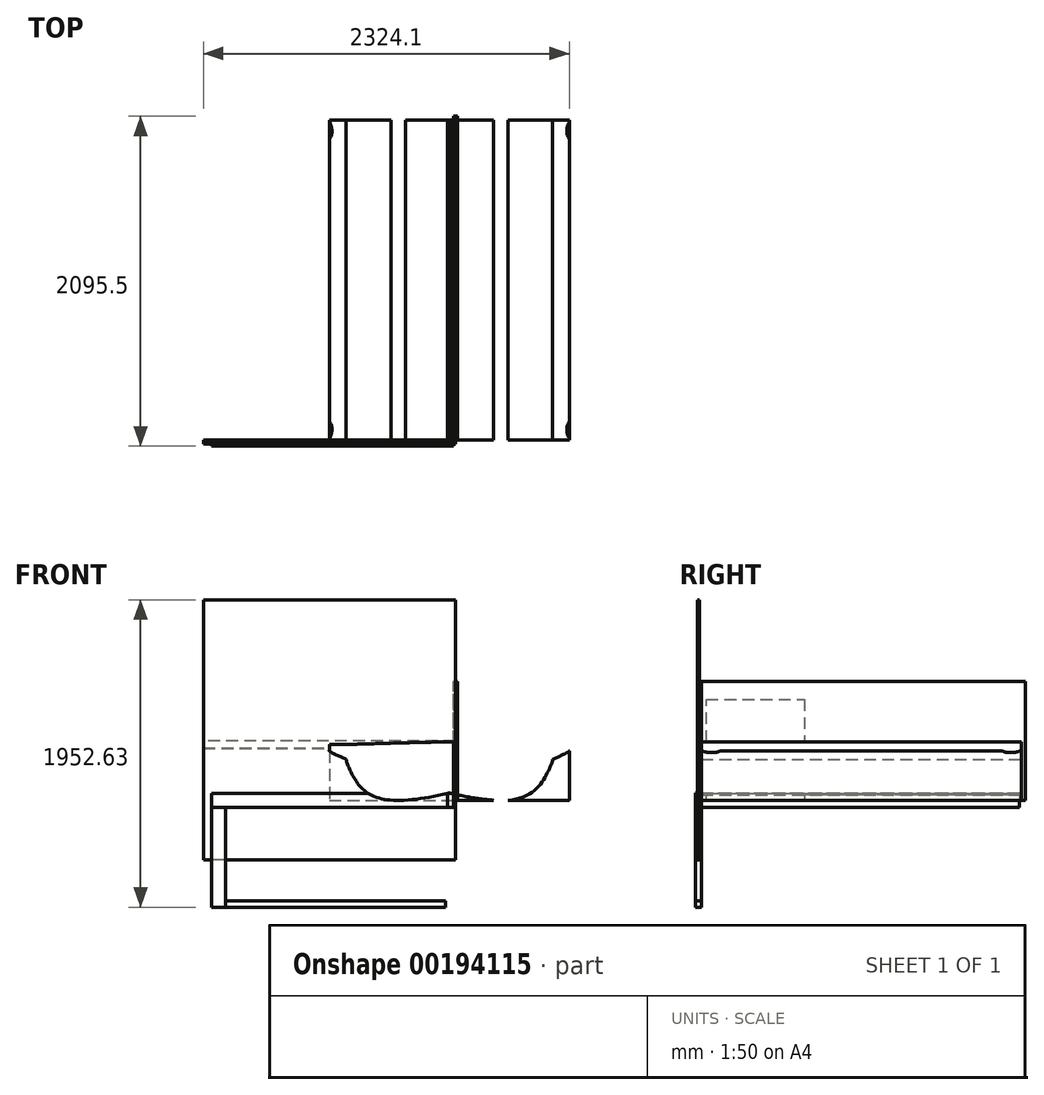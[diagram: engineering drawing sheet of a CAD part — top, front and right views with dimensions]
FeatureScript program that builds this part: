
annotation { "Feature Type Name" : "Feature", "Feature Type Description" : "" }
export const myFeature = defineFeature(function(context is Context, id is Id, definition is map)
    precondition{}
    {
        {
            var Q0;
            Q0=qCreatedBy(makeId("Front.planeOp"),FACE);
            var sketch = newSketch(context, id + "F0", { "sketchPlane" : qUnion([Q0])});
            skLineSegment(sketch, "E0.bottom", {"start": v(749.3, 44.45) * mm, "end": v(-749.3, 44.45) * mm});
            skLineSegment(sketch, "E0.top", {"start": v(749.3, -44.45) * mm, "end": v(-749.3, -44.45) * mm});
            skLineSegment(sketch, "E0.left", {"start": v(749.3, 44.45) * mm, "end": v(749.3, -44.45) * mm});
            skLineSegment(sketch, "E0.right", {"start": v(-749.3, 44.45) * mm, "end": v(-749.3, -44.45) * mm});
            skPoint(sketch, "E0.middle", {"position": v(0, 0) * mm});
            skSolve(sketch);
        }
        {
            var Q0;
            Q0 = qSketchRegion(id + "F0", true);
            extrude(context, id + "F1", {"entities" : qUnion([Q0]), "depth" : 38.1 * mm});
        }
        {
            var Q0;
            Q0=makeQuery(id+"F1.opExtrude","SWEPT_FACE",FACE,{"disambiguationData":[OSD([sQuery(id+"F0.wireOp",EDGE,"E0.left")])]});
            var sketch = newSketch(context, id + "F2", { "sketchPlane" : qUnion([Q0])});
            skLineSegment(sketch, "E1.bottom", {"start": v(-38.1, 44.45) * mm, "end": v(2019.3, 44.45) * mm});
            skLineSegment(sketch, "E1.top", {"start": v(-38.1, -44.45) * mm, "end": v(2019.3, -44.45) * mm});
            skLineSegment(sketch, "E1.left", {"start": v(-38.1, 44.45) * mm, "end": v(-38.1, -44.45) * mm});
            skLineSegment(sketch, "E1.right", {"start": v(2019.3, 44.45) * mm, "end": v(2019.3, -44.45) * mm});
            skSolve(sketch);
        }
        {
            var Q0;
            Q0 = qSketchRegion(id + "F2", true);
            extrude(context, id + "F3", {"entities" : qUnion([Q0]), "depth" : 38.1 * mm});
        }
        {
            var Q0;
            Q0=makeQuery(id+"F1.opExtrude","CAP_FACE",FACE,{"disambiguationData":[OSD([sQuery(id+"F0.wireOp",EDGE,"E0.bottom"),sQuery(id+"F0.wireOp",EDGE,"E0.top"),sQuery(id+"F0.wireOp",EDGE,"E0.left"),sQuery(id+"F0.wireOp",EDGE,"E0.right")])],"isStart":false});
            var sketch = newSketch(context, id + "F4", { "sketchPlane" : qUnion([Q0])});
            skLineSegment(sketch, "E2.bottom", {"start": v(-749.3, -44.45) * mm, "end": v(-660.4, -44.45) * mm});
            skLineSegment(sketch, "E2.top", {"start": v(-749.3, -679.45) * mm, "end": v(-660.4, -679.45) * mm});
            skLineSegment(sketch, "E2.left", {"start": v(-749.3, -44.45) * mm, "end": v(-749.3, -679.45) * mm});
            skLineSegment(sketch, "E2.right", {"start": v(-660.4, -44.45) * mm, "end": v(-660.4, -679.45) * mm});
            skSolve(sketch);
        }
        {
            var Q0;
            Q0 = qSketchRegion(id + "F4", true);
            extrude(context, id + "F5", {"entities" : qUnion([Q0]), "oppositeDirection" : true, "depth" : 38.1 * mm});
        }
        {
            var Q0;
            Q0=makeQuery(id+"F5.opExtrude","CAP_FACE",FACE,{"disambiguationData":[OSD([sQuery(id+"F4.wireOp",EDGE,"E2.bottom"),sQuery(id+"F4.wireOp",EDGE,"E2.top"),sQuery(id+"F4.wireOp",EDGE,"E2.left"),sQuery(id+"F4.wireOp",EDGE,"E2.right")])],"isStart":true});
            var sketch = newSketch(context, id + "F6", { "sketchPlane" : qUnion([Q0])});
            skLineSegment(sketch, "E3.bottom", {"start": v(-660.4, -679.45) * mm, "end": v(736.6, -679.45) * mm});
            skLineSegment(sketch, "E3.top", {"start": v(-660.4, -638.17) * mm, "end": v(736.6, -638.17) * mm});
            skLineSegment(sketch, "E3.left", {"start": v(-660.4, -679.45) * mm, "end": v(-660.4, -638.17) * mm});
            skLineSegment(sketch, "E3.right", {"start": v(736.6, -679.45) * mm, "end": v(736.6, -638.17) * mm});
            skSolve(sketch);
        }
        {
            var Q0;
            Q0=makeQuery(id+"F6.imprint","IMPRINT",FACE,{"disambiguationData":[TD([[makeQuery(id+"F6.imprint","IMPRINT",EDGE,{"derivedFrom":sQuery(id+"F6.wireOp",EDGE,"E3.bottom")}),1.0]])]});
            extrude(context, id + "F7", {"entities" : qUnion([Q0]), "oppositeDirection" : true, "depth" : 38.1 * mm});
        }
        {
            var Q0;
            Q0=makeQuery(id+"F3.opExtrude","CAP_FACE",FACE,{"disambiguationData":[OSD([sQuery(id+"F2.wireOp",EDGE,"E1.bottom"),sQuery(id+"F2.wireOp",EDGE,"E1.top"),sQuery(id+"F2.wireOp",EDGE,"E1.left"),sQuery(id+"F2.wireOp",EDGE,"E1.right")])],"isStart":false});
            var sketch = newSketch(context, id + "F8", { "sketchPlane" : qUnion([Q0])});
            skLineSegment(sketch, "E4", {"start": v(0, 0) * mm, "end": v(0, 755.65) * mm});
            skLineSegment(sketch, "E5", {"start": v(0, 755.65) * mm, "end": v(2057.4, 755.65) * mm});
            skLineSegment(sketch, "E6", {"start": v(0, 0) * mm, "end": v(31.75, 0) * mm});
            skLineSegment(sketch, "E7", {"start": v(31.75, 0) * mm, "end": v(31.75, 641.35) * mm});
            skLineSegment(sketch, "E8", {"start": v(31.75, 641.35) * mm, "end": v(654.05, 641.35) * mm});
            skLineSegment(sketch, "E9", {"start": v(654.05, 641.35) * mm, "end": v(654.05, 0) * mm});
            skLineSegment(sketch, "E10", {"start": v(654.05, 0) * mm, "end": v(2057.4, 0) * mm});
            skPoint(sketch, "E10.endSnap0", {"position": v(2019.3, 0) * mm});
            skLineSegment(sketch, "E11", {"start": v(2057.4, 0) * mm, "end": v(2057.4, 755.65) * mm});
            skSolve(sketch);
        }
        {
            var Q0;
            Q0 = qSketchRegion(id + "F8", true);
            extrude(context, id + "F9", {"entities" : qUnion([Q0]), "depth" : 12.7 * mm});
        }
        {
            var Q0;
            Q0=makeQuery(id+"F9.opExtrude","CAP_FACE",FACE,{"disambiguationData":[OSD([sQuery(id+"F8.wireOp",EDGE,"E4"),sQuery(id+"F8.wireOp",EDGE,"E5"),sQuery(id+"F8.wireOp",EDGE,"E6"),sQuery(id+"F8.wireOp",EDGE,"E7"),sQuery(id+"F8.wireOp",EDGE,"E8"),sQuery(id+"F8.wireOp",EDGE,"E9"),sQuery(id+"F8.wireOp",EDGE,"E10"),sQuery(id+"F8.wireOp",EDGE,"E11")])],"isStart":false});
            var sketch = newSketch(context, id + "F10", { "sketchPlane" : qUnion([Q0])});
            skLineSegment(sketch, "E12.bottom", {"start": v(0, 755.65) * mm, "end": v(2057.4, 755.65) * mm});
            skLineSegment(sketch, "E12.top", {"start": v(0, 0) * mm, "end": v(2057.4, 0) * mm});
            skLineSegment(sketch, "E12.left", {"start": v(0, 755.65) * mm, "end": v(0, 0) * mm});
            skLineSegment(sketch, "E12.right", {"start": v(2057.4, 755.65) * mm, "end": v(2057.4, 0) * mm});
            skSolve(sketch);
        }
        {
            var Q0;
            Q0 = qSketchRegion(id + "F10", true);
            extrude(context, id + "F11", {"entities" : qUnion([Q0]), "depth" : 12.7 * mm});
        }
        {
            var Q0;
            Q0=qCreatedBy(makeId("Front.planeOp"),FACE);
            var sketch = newSketch(context, id + "F12", { "sketchPlane" : qUnion([Q0])});
            skLineSegment(sketch, "E13.bottom", {"start": v(800.1, 377.83) * mm, "end": v(-800.1, 377.83) * mm});
            skLineSegment(sketch, "E13.top", {"start": v(800.1, -377.83) * mm, "end": v(-800.1, -377.83) * mm});
            skLineSegment(sketch, "E13.left", {"start": v(800.1, 377.83) * mm, "end": v(800.1, -377.83) * mm});
            skLineSegment(sketch, "E13.right", {"start": v(-800.1, 377.83) * mm, "end": v(-800.1, -377.83) * mm});
            skPoint(sketch, "E13.middle", {"position": v(0, 0) * mm});
            skSolve(sketch);
        }
        {
            var Q0;
            Q0 = qSketchRegion(id + "F12", true);
            extrude(context, id + "F13", {"entities" : qUnion([Q0]), "depth" : 12.7 * mm});
        }
        {
            var Q0;
            Q0=makeQuery(id+"F13.opExtrude","CAP_FACE",FACE,{"disambiguationData":[OSD([sQuery(id+"F12.wireOp",EDGE,"E13.bottom"),sQuery(id+"F12.wireOp",EDGE,"E13.top"),sQuery(id+"F12.wireOp",EDGE,"E13.left"),sQuery(id+"F12.wireOp",EDGE,"E13.right")])],"isStart":false});
            var sketch = newSketch(context, id + "F14", { "sketchPlane" : qUnion([Q0])});
            skLineSegment(sketch, "E14.bottom", {"start": v(-800.1, -377.83) * mm, "end": v(800.1, -377.83) * mm});
            skLineSegment(sketch, "E14.top", {"start": v(-800.1, 1273.18) * mm, "end": v(800.1, 1273.18) * mm});
            skLineSegment(sketch, "E14.left", {"start": v(-800.1, -377.83) * mm, "end": v(-800.1, 1273.18) * mm});
            skLineSegment(sketch, "E14.right", {"start": v(800.1, -377.83) * mm, "end": v(800.1, 1273.18) * mm});
            skSolve(sketch);
        }
        {
            var Q0;
            Q0 = qSketchRegion(id + "F14", true);
            extrude(context, id + "F15", {"entities" : qUnion([Q0]), "depth" : 12.7 * mm});
        }
        {
            var Q0;
            Q0=makeQuery(id+"F3.opExtrude","SWEPT_FACE",FACE,{"disambiguationData":[OSD([sQuery(id+"F2.wireOp",EDGE,"E1.bottom")])]});
            var sketch = newSketch(context, id + "F16", { "sketchPlane" : qUnion([Q0])});
            skLineSegment(sketch, "E15.bottom", {"start": v(787.4, -38.1) * mm, "end": v(749.3, -38.1) * mm});
            skLineSegment(sketch, "E15.top", {"start": v(787.4, 2019.3) * mm, "end": v(749.3, 2019.3) * mm});
            skLineSegment(sketch, "E15.left", {"start": v(787.4, -38.1) * mm, "end": v(787.4, 2019.3) * mm});
            skLineSegment(sketch, "E15.right", {"start": v(749.3, -38.1) * mm, "end": v(749.3, 2019.3) * mm});
            skSolve(sketch);
        }
        {
            var Q0;
            Q0 = qSketchRegion(id + "F16", true);
            extrude(context, id + "F17", {"entities" : qUnion([Q0]), "depth" : 19.05 * mm});
        }
        {
            var Q0;
            Q0=qCreatedBy(makeId("Top.planeOp"),FACE);
            var sketch = newSketch(context, id + "F18", { "sketchPlane" : qUnion([Q0])});
            skLineSegment(sketch, "E16.bottom", {"start": v(0, 0) * mm, "end": v(1524, 0) * mm});
            skLineSegment(sketch, "E16.top", {"start": v(0, 2032) * mm, "end": v(1524, 2032) * mm});
            skLineSegment(sketch, "E16.left", {"start": v(0, 0) * mm, "end": v(0, 2032) * mm});
            skLineSegment(sketch, "E16.right", {"start": v(1524, 0) * mm, "end": v(1524, 2032) * mm});
            skSolve(sketch);
        }
        {
            var Q0;
            Q0 = qSketchRegion(id + "F18", true);
            extrude(context, id + "F19", {"entities" : qUnion([Q0]), "depth" : 355.6 * mm});
        }
        {
            var Q0;
            Q0=makeQuery(id+"F19.opExtrude","SWEPT_FACE",FACE,{"disambiguationData":[OSD([sQuery(id+"F18.wireOp",EDGE,"E16.top")])]});
            var sketch = newSketch(context, id + "F20", { "sketchPlane" : qUnion([Q0])});
            skLineSegment(sketch, "E17.bottom", {"start": v(-1524, 355.6) * mm, "end": v(-1361.72, 355.6) * mm});
            skLineSegment(sketch, "E17.left", {"start": v(-1524, 355.6) * mm, "end": v(-1524, 319.78) * mm});
            skFitSpline(sketch, "E18", {"points": [v(-1524, 319.78) * mm, v(-1516.64, 336.7) * mm, v(-1478.51, 351.64) * mm, v(-1361.72, 355.6) * mm, v(-135.1, 312.29) * mm, v(-126.97, 200.76) * mm, v(-389.88, 0) * mm, v(-1524, 312.87) * mm, v(-1524, 319.78) * mm]});
            skLineSegment(sketch, "E19", {"start": v(-762, 0) * mm, "end": v(-762, 388.78) * mm, "construction": true});
            skPoint(sketch, "E19.endSnap0", {"position": v(-762, 355.6) * mm});
            skLineSegment(sketch, "E20.MirrorCS", {"start": v(0, 355.6) * mm, "end": v(-162.28, 355.6) * mm});
            skLineSegment(sketch, "E21.MirrorCS", {"start": v(0, 355.6) * mm, "end": v(0, 319.78) * mm});
            skFitSpline(sketch, "E22.MirrorCS", {"points": [v(0, 319.78) * mm, v(-7.36, 336.7) * mm, v(-45.49, 351.64) * mm, v(-162.28, 355.6) * mm, v(-1388.9, 312.29) * mm, v(-1397.03, 200.76) * mm, v(-1134.12, 0) * mm, v(0, 312.87) * mm, v(0, 319.78) * mm]});
            skSolve(sketch);
        }
        {
            var Q0;
            Q0 = qSketchRegion(id + "F20", true);
            extrude(context, id + "F21", {"entities" : qUnion([Q0]), "operationType" : NewBodyOperationType.REMOVE, "endBound" : BoundingType.THROUGH_ALL, "oppositeDirection" : true, "depth" : 25.4 * mm});
        }
        {
            var Q0;
            Q0=makeQuery(id+"F19.opExtrude","SWEPT_FACE",FACE,{"disambiguationData":[OSD([sQuery(id+"F18.wireOp",EDGE,"E16.right")])]});
            var sketch = newSketch(context, id + "F22", { "sketchPlane" : qUnion([Q0])});
            skLineSegment(sketch, "E23.0", {"start": v(0, 355.6) * mm, "end": v(47.79, 355.6) * mm});
            skLineSegment(sketch, "E24", {"start": v(0, 355.6) * mm, "end": v(0, 333.6) * mm});
            skFitSpline(sketch, "E25", {"points": [v(0, 333.6) * mm, v(5.1, 347.61) * mm, v(47.79, 355.6) * mm, v(79.64, 355.6) * mm, v(118.18, 355.6) * mm, v(129.65, 337.42) * mm, v(112.76, 309.4) * mm, v(21.99, 307.48) * mm, v(2.56, 319.78) * mm, v(0, 329.63) * mm, v(0, 333.6) * mm]});
            skPoint(sketch, "E26.trimOffspring.end.orphan", {"position": v(2032, 355.6) * mm});
            skPoint(sketch, "E27.orphan", {"position": v(0, 303.66) * mm});
            skLineSegment(sketch, "E28", {"start": v(1016, 0) * mm, "end": v(1016, 319.78) * mm, "construction": true});
            skLineSegment(sketch, "E29.MirrorCS", {"start": v(2032, 355.6) * mm, "end": v(2032, 333.6) * mm});
            skFitSpline(sketch, "E30.MirrorCS", {"points": [v(2032, 333.6) * mm, v(2026.9, 347.61) * mm, v(1984.21, 355.6) * mm, v(1952.36, 355.6) * mm, v(1913.82, 355.6) * mm, v(1902.35, 337.42) * mm, v(1919.24, 309.4) * mm, v(2010.01, 307.48) * mm, v(2029.44, 319.78) * mm, v(2032, 329.63) * mm, v(2032, 333.6) * mm]});
            skLineSegment(sketch, "E31.MirrorCS", {"start": v(2032, 355.6) * mm, "end": v(1984.21, 355.6) * mm});
            skPoint(sketch, "E32.MirrorP", {"position": v(2032, 303.66) * mm});
            skSolve(sketch);
        }
        {
            var Q0;
            Q0 = qSketchRegion(id + "F22", true);
            extrude(context, id + "F23", {"entities" : qUnion([Q0]), "operationType" : NewBodyOperationType.REMOVE, "endBound" : BoundingType.THROUGH_ALL, "oppositeDirection" : true, "depth" : 25.4 * mm});
        }
    });
